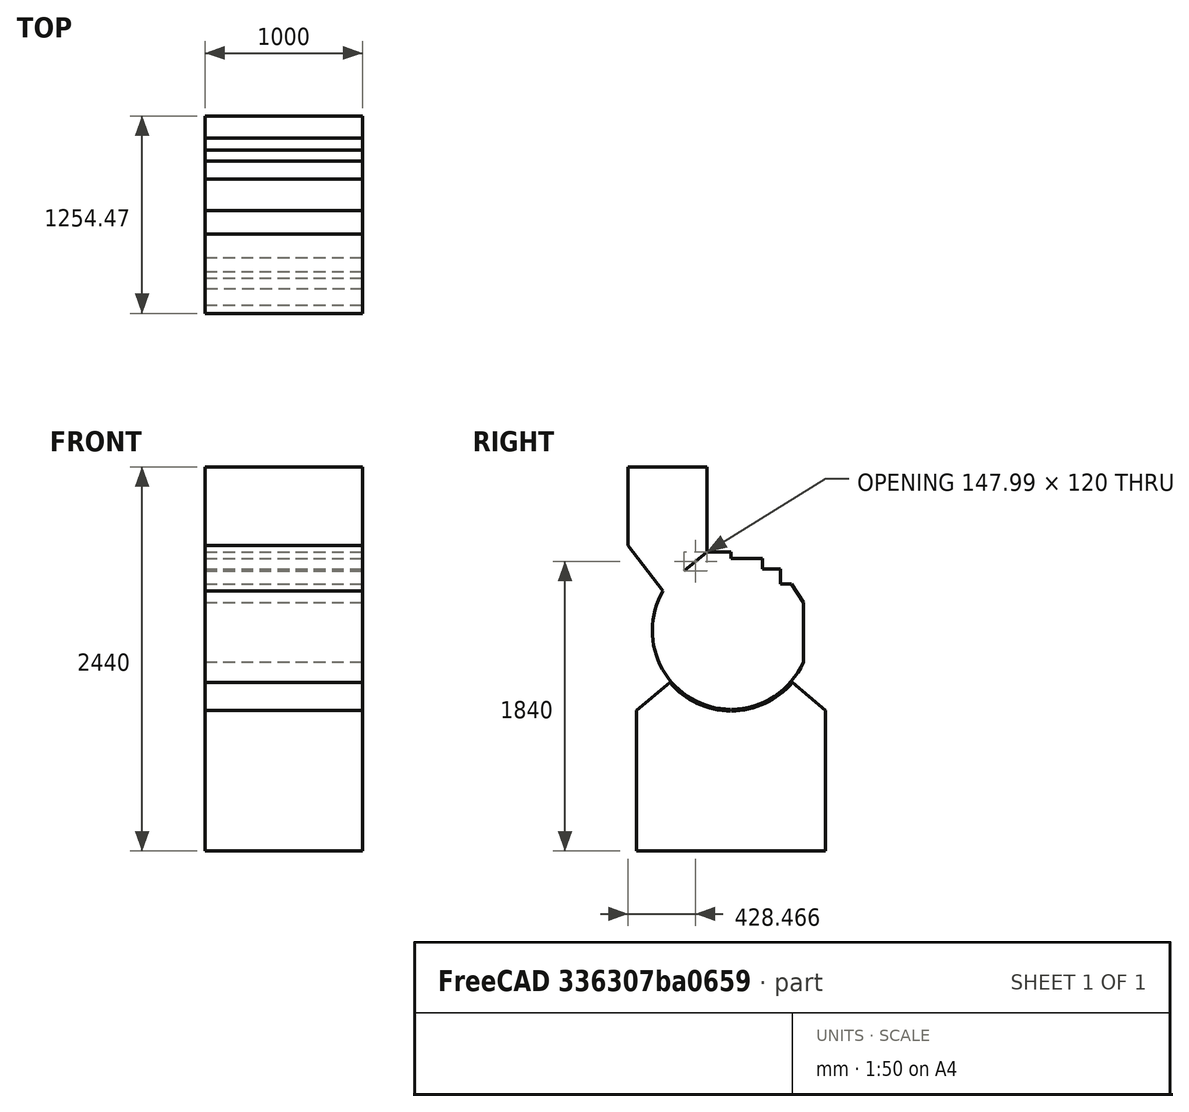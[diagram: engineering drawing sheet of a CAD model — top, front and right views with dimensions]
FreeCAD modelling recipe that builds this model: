
FCSTD DOCUMENT
Label: Shell
objects: Sketcher::SketchObject×1, PartDesign::Pad×1
note: 3 computed .brp shape members not serialized (recipe doc carries the construction recipe); baked Part::Feature solids carry a one-line shape summary decoded from their .brp

FEATURE [Sketcher::SketchObject] Sketch
  Placement = pos=(-500,0,0) rot=(0.57735,0.57735,0.57735;2.0944rad)
  sketch-geometry (25):
    g0: ArcOfCircle CenterX=0 CenterY=0 CenterZ=0 NormalX=0 NormalY=0 NormalZ=1 Radius=500 StartAngle=2.61058 EndAngle=4.70765
    g1: LineSegment StartX=-431.147 StartY=253.204 StartZ=0 EndX=-654.474 EndY=540 EndZ=0
    g2: LineSegment StartX=-152.007 StartY=500 StartZ=0 EndX=-0.000226751 EndY=500 EndZ=0
    g3: LineSegment StartX=-0.000226751 StartY=500 StartZ=0 EndX=-0.000226751 EndY=458.471 EndZ=0
    g4: LineSegment StartX=-0.000226751 StartY=458.471 StartZ=0 EndX=199.509 EndY=458.471 EndZ=0
    g5: LineSegment StartX=199.509 StartY=458.471 StartZ=0 EndX=199.509 EndY=390 EndZ=0
    g6: LineSegment StartX=199.509 StartY=390 StartZ=0 EndX=312.89 EndY=390 EndZ=0
    g7: LineSegment StartX=312.89 StartY=390 StartZ=0 EndX=312.89 EndY=297.137 EndZ=0
    g8: LineSegment StartX=312.89 StartY=297.137 StartZ=0 EndX=382.89 EndY=297.137 EndZ=0
    g9: LineSegment StartX=458.29 StartY=180.074 StartZ=0 EndX=458.29 EndY=-199.926 EndZ=0
    g10: LineSegment StartX=-654.474 StartY=1040 StartZ=0 EndX=-654.474 EndY=540 EndZ=0
    g11: LineSegment StartX=-152.007 StartY=500 StartZ=0 EndX=-300 EndY=380 EndZ=0
    g12: LineSegment StartX=-388.591 StartY=-330.298 StartZ=0 EndX=-600 EndY=-507.691 EndZ=0
    g13: LineSegment StartX=-600 StartY=-507.691 StartZ=0 EndX=-600 EndY=-1400 EndZ=0
    g14: LineSegment StartX=-600 StartY=-1400 StartZ=0 EndX=600 EndY=-1400 EndZ=0
    g15: LineSegment StartX=600 StartY=-1400 StartZ=0 EndX=600 EndY=-507.691 EndZ=0
    g16: LineSegment StartX=600 StartY=-507.691 StartZ=0 EndX=388.591 EndY=-330.298 EndZ=0
    g17: LineSegment StartX=382.89 StartY=297.137 StartZ=0 EndX=458.29 EndY=180.074 EndZ=0
    g18: ArcOfCircle CenterX=0 CenterY=0 CenterZ=0 NormalX=0 NormalY=0 NormalZ=1 Radius=510 StartAngle=3.84608 EndAngle=4.70774
    g19: LineSegment StartX=-2.36852 StartY=-499.994 StartZ=0 EndX=-2.36852 EndY=-509.995 EndZ=0
    g20: LineSegment StartX=2.36852 StartY=-499.994 StartZ=0 EndX=2.36852 EndY=-509.995 EndZ=0
    g21: ArcOfCircle CenterX=0 CenterY=0 CenterZ=0 NormalX=0 NormalY=0 NormalZ=1 Radius=500 StartAngle=4.71713 EndAngle=5.87183
    g22: ArcOfCircle CenterX=0 CenterY=0 CenterZ=0 NormalX=0 NormalY=0 NormalZ=1 Radius=510 StartAngle=4.71703 EndAngle=5.5787
    g23: LineSegment StartX=-654.474 StartY=1040 StartZ=0 EndX=-152.007 EndY=1040 EndZ=0
    g24: LineSegment StartX=-152.007 StartY=1040 StartZ=0 EndX=-152.007 EndY=500 EndZ=0
  constraints (77):
    c: Radius(g0) = 500
    c: DistanceX(g0) = 0
    c: DistanceY(g0) = 0
    c: PointOnObject(g3,g0)
    c: Horizontal(g2)
    c: Vertical(g3)
    c: Coincident(g4,g3)
    c: PointOnObject(g5,g0)
    c: Horizontal(g4)
    c: Vertical(g5)
    c: Coincident(g6,g5)
    c: PointOnObject(g7,g0)
    c: Horizontal(g6)
    c: Vertical(g7)
    c: Coincident(g8,g7)
    c: Horizontal(g8)
    c: DistanceX(g1) = -654.474
    c: DistanceY(g1) = 540
    c: Coincident(g2,g3)
    c: Coincident(g4,g5)
    c: Coincident(g6,g7)
    c: Coincident(g9,g21)
    c: Vertical(g9)
    c: Distance(g9) = 380
    c: DistanceX(g2) = -152.007
    c: DistanceY(g2) = 500
    c: DistanceX(g5) = 199.509
    c: DistanceY(g5) = 390
    c: Distance(g8) = 70
    c: Coincident(g1,g0)
    c: Coincident(g10,g1)
    c: Vertical(g10)
    c: DistanceX(g11) = -300
    c: DistanceY(g11) = 380
    c: Distance(g1) = 363.493
    c: Coincident(g11,g2)
    c: Distance(g10) = 500
    c: Coincident(g13,g12)
    c: Vertical(g13)
    c: Horizontal(g14)
    c: Coincident(g15,g14)
    c: Vertical(g15)
    c: Coincident(g16,g15)
    c: Coincident(g14,g13)
    c: Equal(g15,g13)
    c: DistanceX(g14) = 600
    c: DistanceY(g14) = -1400
    c: Angle(g13,g12) = 2.26893
    c: Angle(g16,g15) = 2.26893
    c: Distance(g13) = 892.309
    c: Distance(g14) = 1200
    c: Coincident(g17,g8)
    c: Coincident(g17,g9)
    c: Distance(g17) = 139.244
    c: Distance(g7) = 92.8633
    c: Radius(g18) = 510
    c: DistanceX(g18) = 0
    c: DistanceY(g18) = 0
    c: Coincident(g18,g12)
    c: Coincident(g16,g22)
    c: Vertical(g19)
    c: Equal(g20,g19)
    c: Equal(g0,g21)
    c: Coincident(g0,g19)
    c: Coincident(g21,g20)
    c: Coincident(g0,g21)
    c: Equal(g18,g22)
    c: Coincident(g18,g19)
    c: Coincident(g22,g20)
    c: Coincident(g18,g22)
    c: Vertical(g20)
    c: Distance(g19) = 10.0001
    c: Coincident(g23,g10)
    c: Horizontal(g23)
    c: Coincident(g24,g23)
    c: Coincident(g24,g2)
    c: Vertical(g24)
FEATURE [PartDesign::Pad] Pad
  Length = 1000
  MirroredExtent = false
  Sketch = -> Sketch
